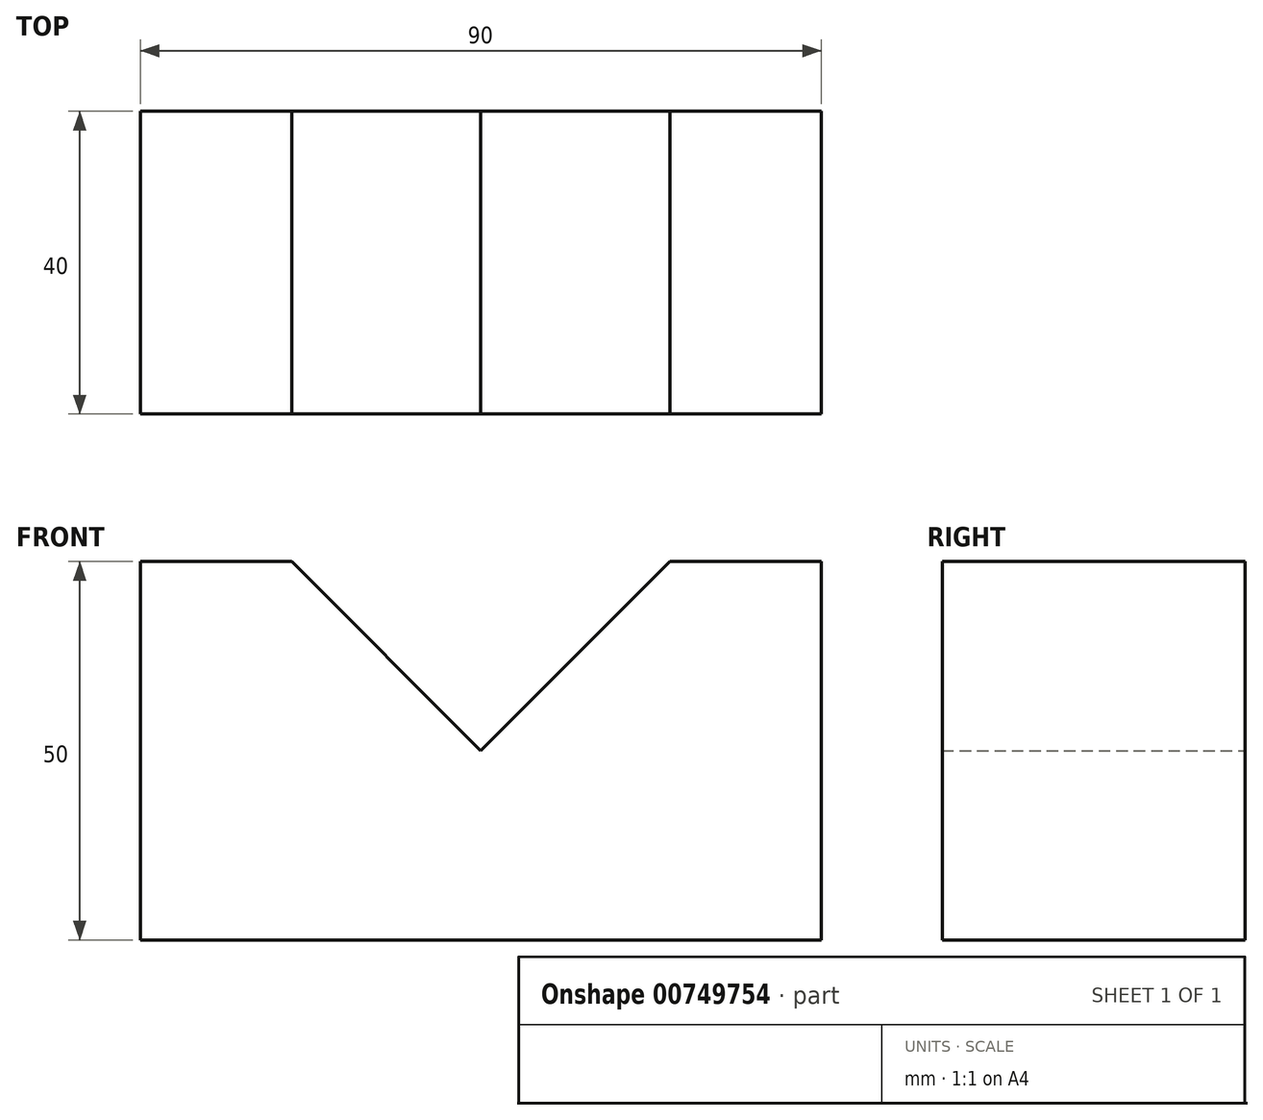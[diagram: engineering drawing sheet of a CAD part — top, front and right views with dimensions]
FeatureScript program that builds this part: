
annotation { "Feature Type Name" : "Feature", "Feature Type Description" : "" }
export const myFeature = defineFeature(function(context is Context, id is Id, definition is map)
    precondition{}
    {
        {
            var Q0;
            Q0=qCreatedBy(makeId("Front.planeOp"),FACE);
            var sketch = newSketch(context, id + "F0", { "sketchPlane" : qUnion([Q0])});
            skLineSegment(sketch, "E0", {"start": v(-27.33, -10.99) * mm, "end": v(62.67, -10.99) * mm});
            skLineSegment(sketch, "E1", {"start": v(62.67, -10.99) * mm, "end": v(62.67, 39.01) * mm});
            skPoint(sketch, "E2.endSnap0", {"position": v(17.67, -10.99) * mm});
            skLineSegment(sketch, "E3", {"start": v(-27.33, 39.01) * mm, "end": v(-27.33, -10.99) * mm});
            skLineSegment(sketch, "E4", {"start": v(-27.33, 39.01) * mm, "end": v(-7.33, 39.01) * mm});
            skLineSegment(sketch, "E5", {"start": v(-7.33, 39.01) * mm, "end": v(17.67, 14.01) * mm});
            skLineSegment(sketch, "E6", {"start": v(17.67, 14.01) * mm, "end": v(42.67, 39.01) * mm});
            skLineSegment(sketch, "E7", {"start": v(42.67, 39.01) * mm, "end": v(62.67, 39.01) * mm});
            skSolve(sketch);
        }
        {
            var Q0;
            Q0 = qSketchRegion(id + "F0", true);
            extrude(context, id + "F1", {"entities" : qUnion([Q0]), "endBound" : BoundingType.SYMMETRIC, "depth" : 40 * mm, "offsetDistance" : 25.4 * mm});
        }
    });
